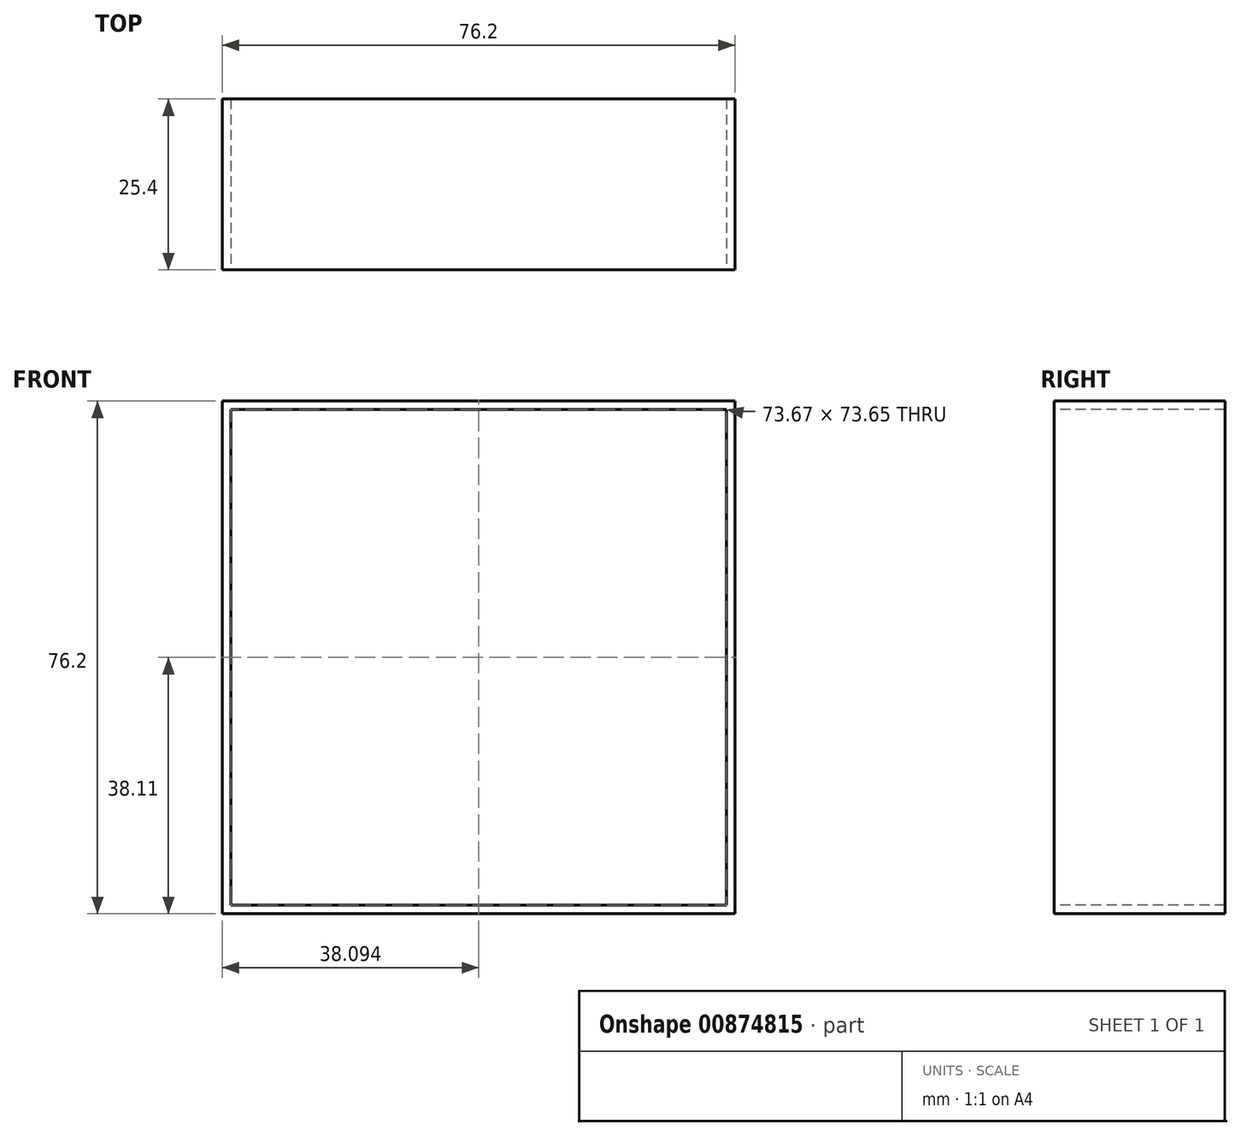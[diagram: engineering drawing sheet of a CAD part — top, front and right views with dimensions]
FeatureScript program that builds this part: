
annotation { "Feature Type Name" : "Feature", "Feature Type Description" : "" }
export const myFeature = defineFeature(function(context is Context, id is Id, definition is map)
    precondition{}
    {
        {
            var Q0;
            Q0=qCreatedBy(makeId("Front.planeOp"),FACE);
            var sketch = newSketch(context, id + "F0", { "sketchPlane" : qUnion([Q0])});
            skLineSegment(sketch, "E0.bottom", {"start": v(-117.25, 89.57) * mm, "end": v(-41.05, 89.57) * mm});
            skLineSegment(sketch, "E0.top", {"start": v(-117.25, 13.37) * mm, "end": v(-41.05, 13.37) * mm});
            skLineSegment(sketch, "E0.left", {"start": v(-117.25, 89.57) * mm, "end": v(-117.25, 13.37) * mm});
            skLineSegment(sketch, "E0.right", {"start": v(-41.05, 89.57) * mm, "end": v(-41.05, 13.37) * mm});
            skSolve(sketch);
        }
        {
            var Q0;
            Q0=qSketchRegion(id+"F0",true);
            extrude(context, id + "F1", {"entities" : qUnion([Q0]), "depth" : 609.6 * mm, "offsetDistance" : 25.4 * mm});
        }
        {
            var Q0;
            Q0=makeQuery(id+"F1.opExtrude","CAP_FACE",FACE,{"disambiguationData":[OSD([sQuery(id+"F0.wireOp",EDGE,"E0.bottom"),sQuery(id+"F0.wireOp",EDGE,"E0.top"),sQuery(id+"F0.wireOp",EDGE,"E0.left"),sQuery(id+"F0.wireOp",EDGE,"E0.right")])],"isStart":false});
            var sketch = newSketch(context, id + "F2", { "sketchPlane" : qUnion([Q0])});
            skLineSegment(sketch, "E1", {"start": v(-98.69, 89.57) * mm, "end": v(-98.69, 88.3) * mm});
            skLineSegment(sketch, "E2", {"start": v(-98.69, 88.3) * mm, "end": v(-116, 88.3) * mm});
            skLineSegment(sketch, "E3", {"start": v(-116, 88.3) * mm, "end": v(-116, 14.66) * mm});
            skLineSegment(sketch, "E4", {"start": v(-116, 14.66) * mm, "end": v(-42.32, 14.66) * mm});
            skLineSegment(sketch, "E5", {"start": v(-42.32, 14.66) * mm, "end": v(-42.32, 88.3) * mm});
            skLineSegment(sketch, "E6", {"start": v(-42.32, 88.3) * mm, "end": v(-98.69, 88.3) * mm});
            skSolve(sketch);
        }
        {
            var Q0;
            Q0=makeQuery(id+"F2.imprint","IMPRINT",FACE,{"disambiguationData":[TD([[makeQuery(id+"F2.imprint","IMPRINT",EDGE,{"derivedFrom":sQuery(id+"F2.wireOp",EDGE,"E2")}),1.0]])]});
            extrude(context, id + "F3", {"entities" : qUnion([Q0]), "operationType" : NewBodyOperationType.REMOVE, "oppositeDirection" : true, "depth" : 914.4 * mm, "offsetDistance" : 25.4 * mm});
        }
        {
            var Q0;
            Q0=makeQuery(id+"F1.opExtrude","CAP_FACE",FACE,{"disambiguationData":[OSD([sQuery(id+"F0.wireOp",EDGE,"E0.bottom"),sQuery(id+"F0.wireOp",EDGE,"E0.top"),sQuery(id+"F0.wireOp",EDGE,"E0.left"),sQuery(id+"F0.wireOp",EDGE,"E0.right")])],"isStart":false});
            extrude(context, id + "F4", {"entities" : qUnion([Q0]), "operationType" : NewBodyOperationType.ADD, "depth" : 304.8 * mm, "offsetDistance" : 25.4 * mm});
        }
        {
            var Q0;
            Q0=makeQuery(id+"F1.opExtrude","CAP_FACE",FACE,{"disambiguationData":[OSD([sQuery(id+"F0.wireOp",EDGE,"E0.bottom"),sQuery(id+"F0.wireOp",EDGE,"E0.top"),sQuery(id+"F0.wireOp",EDGE,"E0.left"),sQuery(id+"F0.wireOp",EDGE,"E0.right")])],"isStart":true});
            extrude(context, id + "F5", {"entities" : qUnion([Q0]), "operationType" : NewBodyOperationType.REMOVE, "oppositeDirection" : true, "depth" : 508 * mm, "offsetDistance" : 25.4 * mm});
        }
        {
            var Q0;
            Q0=makeQuery(id+"F5.boolean.opBoolean","COPY",FACE,{"derivedFrom":makeQuery(id+"F5.opExtrude","CAP_FACE",FACE,{"disambiguationData":[OSD([sQuery(id+"F0.wireOp",EDGE,"E0.bottom"),sQuery(id+"F0.wireOp",EDGE,"E0.top"),sQuery(id+"F0.wireOp",EDGE,"E0.left"),sQuery(id+"F0.wireOp",EDGE,"E0.right")])],"isStart":false})});
            extrude(context, id + "F6", {"entities" : qUnion([Q0]), "operationType" : NewBodyOperationType.REMOVE, "oppositeDirection" : true, "depth" : 381 * mm, "offsetDistance" : 25.4 * mm});
        }
    });
